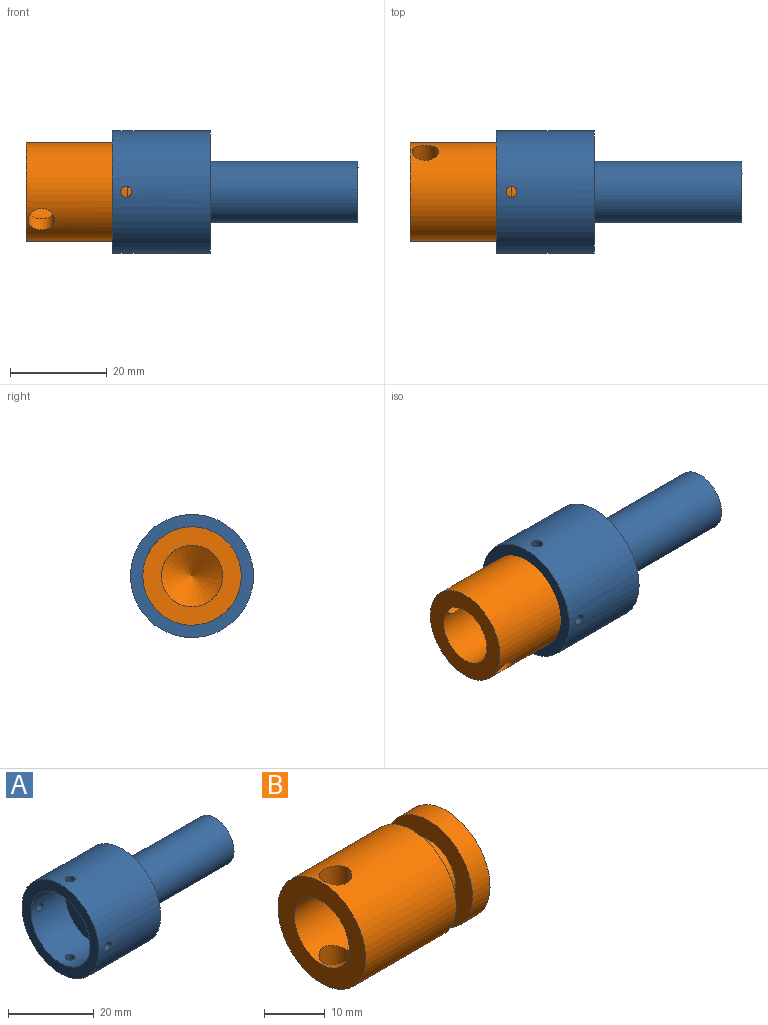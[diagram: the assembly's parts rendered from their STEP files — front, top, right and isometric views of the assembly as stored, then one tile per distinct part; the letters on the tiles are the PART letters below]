
ASSEMBLY  parts=2 mates=1
PART A: 12 faces, bbox 50.8x25.4x25.4 mm
  f0: cylinder r=9.72mm len=19.44mm, axis (-1,0,0), area 661.6mm2, adj f2,f7,f8,f9,f10,f11
  f1: cylinder r=12.7mm len=25.4mm, axis (-1,0,0), area 1606.4mm2, adj f6,f7,f8,f9,f10,f11
  f2: plane 19.44x19.44mm, normal (-1,0,0), area 236.6mm2, adj f0,f3
  f3: revolved ~8.76x8.76mm, area 97.4mm2, adj f2
  f4: plane 12.7x12.7mm, normal (1,0,0), area 126.7mm2, adj f5
  f5: cylinder r=6.35mm len=30.47mm, axis (-1,0,0), area 1215.6mm2, adj f4,f6
  f6: plane 25.4x25.4mm, normal (1,0,0), area 380mm2, adj f1,f5
  f7: plane 25.4x25.4mm, normal (-1,0,0), area 209.8mm2, adj f0,f1
  f8: cylinder r=1.13mm len=3.04mm, axis (0,0,-1), area 21.2mm2, adj f0,f1
  f9: cylinder r=1.13mm len=3.04mm, axis (0,0,-1), area 21.2mm2, adj f0,f1
  f10: cylinder r=1.13mm len=3.05mm, axis (0,-1,0), area 21.2mm2, adj f0,f1
  f11: cylinder r=1.13mm len=3.05mm, axis (0,-1,0), area 21.2mm2, adj f0,f1
PART B: 12 faces, bbox 49.2x40.6x40.6 mm
  f0: cylinder r=6.35mm len=15.82mm, axis (-1,0,0), area 584.2mm2, adj f2,f9,f10,f11
  f1: cylinder r=10.16mm len=21.04mm, axis (-1,0,0), area 1296.9mm2, adj f8,f9,f10,f11
  f2: cone r=6.35mm half-angle=55.1deg, axis (-1,0,0), area 154.4mm2, adj f0
  f3: revolved ~10.16x5.08mm, area 0mm2, adj f4
  f4: plane 40.64x40.64mm, normal (1,0,0), area 243.2mm2, adj f3,f5
  f5: cylinder r=10.16mm len=20.32mm, axis (-1,0,0), area 260.7mm2, adj f4,f6
  f6: plane 20.32x20.32mm, normal (-1,0,0), area 197.6mm2, adj f5,f7
  f7: cylinder r=6.35mm len=12.7mm, axis (-1,0,0), area 149.4mm2, adj f6,f8
  f8: plane 20.32x20.32mm, normal (1,0,0), area 197.6mm2, adj f1,f7
  f9: plane 20.32x20.32mm, normal (-1,0,0), area 197.6mm2, adj f0,f1
  f10: cylinder r=2.71mm len=5.41mm, axis (0,0,1), area 66.7mm2, adj f0,f1
  f11: cylinder r=2.71mm len=5.41mm, axis (0,0,1), area 66.7mm2, adj f0,f1
PLACE A rot(axis=(-0.83,0.47,-0.32),0deg) t=(31.06,-1.39,-21.41)mm fixed
PLACE B rot(axis=(-1,0,0),55.2deg) t=(29.01,-1.39,-8.71)mm
MATE revolute A.f0 <-> B.f0  axis (-1,0,0) through (57.88,-1.39,-8.71)mm
